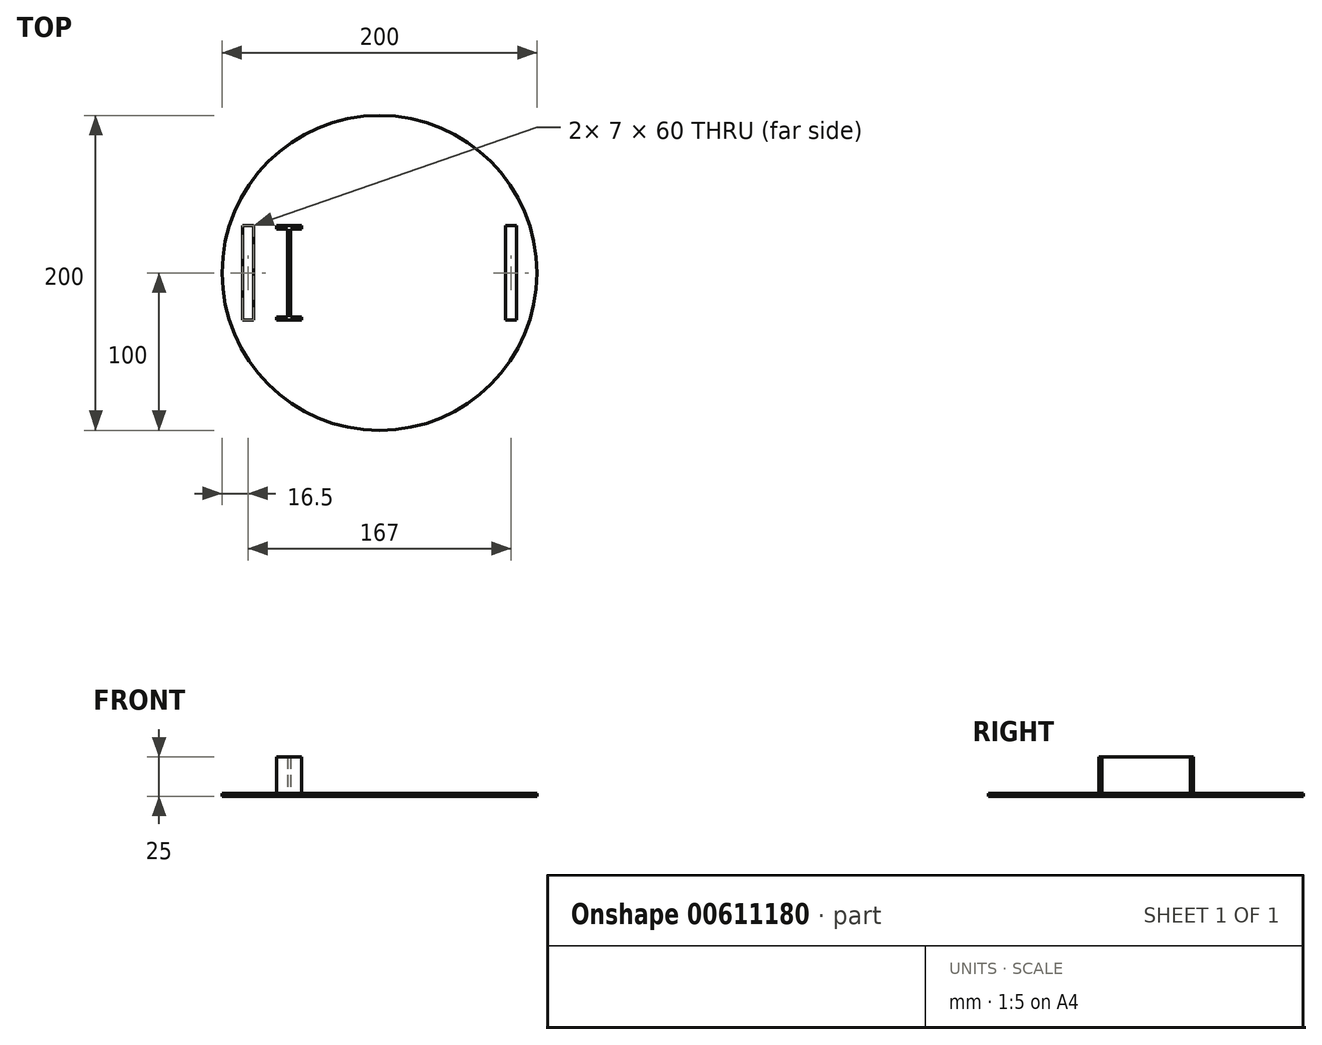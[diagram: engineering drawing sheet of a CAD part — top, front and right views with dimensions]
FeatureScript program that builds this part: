
annotation { "Feature Type Name" : "Feature", "Feature Type Description" : "" }
export const myFeature = defineFeature(function(context is Context, id is Id, definition is map)
    precondition{}
    {
        {
            var Q0;
            Q0=qCreatedBy(makeId("Top.planeOp"),FACE);
            var sketch = newSketch(context, id + "F0", { "sketchPlane" : qUnion([Q0])});
            skCircle(sketch, "E0", {"center": v(0, 0) * mm, "radius": 100 * mm});
            skLineSegment(sketch, "E1.bottom", {"start": v(-80, 30) * mm, "end": v(-87, 30) * mm});
            skLineSegment(sketch, "E1.top", {"start": v(-80, -30) * mm, "end": v(-87, -30) * mm});
            skLineSegment(sketch, "E1.left", {"start": v(-80, 30) * mm, "end": v(-80, -30) * mm});
            skLineSegment(sketch, "E1.right", {"start": v(-87, 30) * mm, "end": v(-87, -30) * mm});
            skPoint(sketch, "E1.middle", {"position": v(-83.5, 0) * mm});
            skLineSegment(sketch, "E2.MirrorCS", {"start": v(80, 30) * mm, "end": v(87, 30) * mm});
            skLineSegment(sketch, "E3.MirrorCS", {"start": v(80, 30) * mm, "end": v(80, -30) * mm});
            skLineSegment(sketch, "E4.MirrorCS", {"start": v(80, -30) * mm, "end": v(87, -30) * mm});
            skLineSegment(sketch, "E5.MirrorCS", {"start": v(87, 30) * mm, "end": v(87, -30) * mm});
            skPoint(sketch, "E6.MirrorP", {"position": v(83.5, 0) * mm});
            skLineSegment(sketch, "E7.bottom", {"start": v(-56.5, 30) * mm, "end": v(-58.5, 30) * mm});
            skLineSegment(sketch, "E7.left", {"start": v(-56.5, 30) * mm, "end": v(-56.5, -30) * mm});
            skLineSegment(sketch, "E7.right", {"start": v(-58.5, 30) * mm, "end": v(-58.5, -30) * mm});
            skPoint(sketch, "E7.middle", {"position": v(-57.5, 0) * mm});
            skLineSegment(sketch, "E8.bottom", {"start": v(-65.5, 28) * mm, "end": v(-49.5, 28) * mm});
            skLineSegment(sketch, "E8.top", {"start": v(-65.5, 30) * mm, "end": v(-49.5, 30) * mm});
            skLineSegment(sketch, "E8.left", {"start": v(-65.5, 28) * mm, "end": v(-65.5, 30) * mm});
            skLineSegment(sketch, "E8.right", {"start": v(-49.5, 28) * mm, "end": v(-49.5, 30) * mm});
            skLineSegment(sketch, "E9.MirrorCS", {"start": v(-56.5, -30) * mm, "end": v(-58.5, -30) * mm});
            skLineSegment(sketch, "E10.MirrorCS", {"start": v(-65.5, -30) * mm, "end": v(-49.5, -30) * mm});
            skLineSegment(sketch, "E11.MirrorCS", {"start": v(-65.5, -28) * mm, "end": v(-49.5, -28) * mm});
            skLineSegment(sketch, "E12.MirrorCS", {"start": v(-49.5, -28) * mm, "end": v(-49.5, -30) * mm});
            skLineSegment(sketch, "E13.MirrorCS", {"start": v(-65.5, -28) * mm, "end": v(-65.5, -30) * mm});
            skSolve(sketch);
        }
        {
            var Q0;
            {var subQ0=sQuery(id+"F0.wireOp",EDGE,"K0GAp1Y4-Ixp0-aC1l-omNU-r5FszGDL7PR0.top");var subQ1=sQuery(id+"F0.wireOp",EDGE,"HqlQ3rIF-Y2ew-o2BC-WH6p-pxuWtE5EoVCb.left");var subQ2=makeQuery(id+"F0.imprint","INTERSECT",VERTEX,{"derivedFrom":[subQ1,subQ0]});Q0=makeQuery(id+"F0.imprint","IMPRINT",FACE,{"disambiguationData":[TD([[makeQuery(id+"F0.imprint","IMPRINT",EDGE,{"disambiguationData":[TD([[subQ2,-1.0]])],"derivedFrom":subQ1}),-1.0]])]});}
            var Q1;
            {var subQ5=sQuery(id+"F0.wireOp",EDGE,"K0GAp1Y4-Ixp0-aC1l-omNU-r5FszGDL7PR0.right");Q1=makeQuery(id+"F0.imprint","IMPRINT",FACE,{"disambiguationData":[TD([[makeQuery(id+"F0.imprint","IMPRINT",EDGE,{"derivedFrom":subQ5}),1.0]])]});}
            var Q2;
            {var subQ5=sQuery(id+"F0.wireOp",EDGE,"K0GAp1Y4-Ixp0-aC1l-omNU-r5FszGDL7PR0.left");Q2=makeQuery(id+"F0.imprint","IMPRINT",FACE,{"disambiguationData":[TD([[makeQuery(id+"F0.imprint","IMPRINT",EDGE,{"derivedFrom":subQ5}),-1.0]])]});}
            var Q3;
            {var subQ0=sQuery(id+"F0.wireOp",EDGE,"K0GAp1Y4-Ixp0-aC1l-omNU-r5FszGDL7PR0.bottom");var subQ1=sQuery(id+"F0.wireOp",EDGE,"HqlQ3rIF-Y2ew-o2BC-WH6p-pxuWtE5EoVCb.left");var subQ2=makeQuery(id+"F0.imprint","INTERSECT",VERTEX,{"derivedFrom":[subQ1,subQ0]});Q3=makeQuery(id+"F0.imprint","IMPRINT",FACE,{"disambiguationData":[TD([[makeQuery(id+"F0.imprint","IMPRINT",EDGE,{"disambiguationData":[TD([[subQ2,-1.0]])],"derivedFrom":subQ1}),-1.0]])]});}
            var Q4;
            Q4=makeQuery(id+"F0.imprint","IMPRINT",FACE,{"disambiguationData":[TD([[makeQuery(id+"F0.imprint","IMPRINT",EDGE,{"derivedFrom":sQuery(id+"F0.wireOp",EDGE,"E0")}),1.0]])]});
            var Q5;
            {var subQ5=sQuery(id+"F0.wireOp",EDGE,"2bd450b3-5e51-421b-8461-b64049ee1ff72.MirrorCS");Q5=makeQuery(id+"F0.imprint","IMPRINT",FACE,{"disambiguationData":[TD([[makeQuery(id+"F0.imprint","IMPRINT",EDGE,{"derivedFrom":subQ5}),-1.0]])]});}
            var Q6;
            {var subQ0=sQuery(id+"F0.wireOp",EDGE,"2bd450b3-5e51-421b-8461-b64049ee1ff74.MirrorCS");var subQ1=sQuery(id+"F0.wireOp",EDGE,"HqlQ3rIF-Y2ew-o2BC-WH6p-pxuWtE5EoVCb.left");var subQ2=makeQuery(id+"F0.imprint","INTERSECT",VERTEX,{"derivedFrom":[subQ1,subQ0]});Q6=makeQuery(id+"F0.imprint","IMPRINT",FACE,{"disambiguationData":[TD([[makeQuery(id+"F0.imprint","IMPRINT",EDGE,{"disambiguationData":[TD([[subQ2,1.0]])],"derivedFrom":subQ1}),-1.0]])]});}
            var Q7;
            {var subQ5=sQuery(id+"F0.wireOp",EDGE,"2bd450b3-5e51-421b-8461-b64049ee1ff70.MirrorCS");Q7=makeQuery(id+"F0.imprint","IMPRINT",FACE,{"disambiguationData":[TD([[makeQuery(id+"F0.imprint","IMPRINT",EDGE,{"derivedFrom":subQ5}),1.0]])]});}
            var Q8;
            {var subQ5=sQuery(id+"F0.wireOp",EDGE,"E13.MirrorCS");Q8=makeQuery(id+"F0.imprint","IMPRINT",FACE,{"disambiguationData":[TD([[makeQuery(id+"F0.imprint","IMPRINT",EDGE,{"derivedFrom":subQ5}),1.0]])]});}
            var Q9;
            {var subQ0=sQuery(id+"F0.wireOp",EDGE,"E10.MirrorCS");var subQ1=sQuery(id+"F0.wireOp",EDGE,"E7.left");var subQ2=makeQuery(id+"F0.imprint","INTERSECT",VERTEX,{"derivedFrom":[subQ1,subQ0]});Q9=makeQuery(id+"F0.imprint","IMPRINT",FACE,{"disambiguationData":[TD([[makeQuery(id+"F0.imprint","IMPRINT",EDGE,{"disambiguationData":[TD([[subQ2,1.0]])],"derivedFrom":subQ1}),-1.0]])]});}
            var Q10;
            {var subQ5=sQuery(id+"F0.wireOp",EDGE,"E12.MirrorCS");Q10=makeQuery(id+"F0.imprint","IMPRINT",FACE,{"disambiguationData":[TD([[makeQuery(id+"F0.imprint","IMPRINT",EDGE,{"derivedFrom":subQ5}),-1.0]])]});}
            var Q11;
            {var subQ0=sQuery(id+"F0.wireOp",EDGE,"E8.bottom");var subQ1=sQuery(id+"F0.wireOp",EDGE,"E7.left");var subQ2=makeQuery(id+"F0.imprint","INTERSECT",VERTEX,{"derivedFrom":[subQ1,subQ0]});Q11=makeQuery(id+"F0.imprint","IMPRINT",FACE,{"disambiguationData":[TD([[makeQuery(id+"F0.imprint","IMPRINT",EDGE,{"disambiguationData":[TD([[subQ2,-1.0]])],"derivedFrom":subQ1}),-1.0]])]});}
            var Q12;
            {var subQ5=sQuery(id+"F0.wireOp",EDGE,"E8.left");Q12=makeQuery(id+"F0.imprint","IMPRINT",FACE,{"disambiguationData":[TD([[makeQuery(id+"F0.imprint","IMPRINT",EDGE,{"derivedFrom":subQ5}),-1.0]])]});}
            var Q13;
            {var subQ0=sQuery(id+"F0.wireOp",EDGE,"E8.top");var subQ1=sQuery(id+"F0.wireOp",EDGE,"E7.left");var subQ2=makeQuery(id+"F0.imprint","INTERSECT",VERTEX,{"derivedFrom":[subQ1,subQ0]});Q13=makeQuery(id+"F0.imprint","IMPRINT",FACE,{"disambiguationData":[TD([[makeQuery(id+"F0.imprint","IMPRINT",EDGE,{"disambiguationData":[TD([[subQ2,-1.0]])],"derivedFrom":subQ1}),-1.0]])]});}
            var Q14;
            {var subQ5=sQuery(id+"F0.wireOp",EDGE,"E8.right");Q14=makeQuery(id+"F0.imprint","IMPRINT",FACE,{"disambiguationData":[TD([[makeQuery(id+"F0.imprint","IMPRINT",EDGE,{"derivedFrom":subQ5}),1.0]])]});}
            extrude(context, id + "F1", {"entities" : qUnion([Q0, Q1, Q2, Q3, Q4, Q5, Q6, Q7, Q8, Q9, Q10, Q11, Q12, Q13, Q14]), "depth" : 2 * mm, "offsetDistance" : 25.4 * mm});
        }
        {
            var Q0;
            {var subQ5=sQuery(id+"F0.wireOp",EDGE,"E8.left");Q0=makeQuery(id+"F0.imprint","IMPRINT",FACE,{"disambiguationData":[TD([[makeQuery(id+"F0.imprint","IMPRINT",EDGE,{"derivedFrom":subQ5}),-1.0]])]});}
            var Q1;
            {var subQ0=sQuery(id+"F0.wireOp",EDGE,"E8.top");var subQ1=sQuery(id+"F0.wireOp",EDGE,"E7.left");var subQ2=makeQuery(id+"F0.imprint","INTERSECT",VERTEX,{"derivedFrom":[subQ1,subQ0]});Q1=makeQuery(id+"F0.imprint","IMPRINT",FACE,{"disambiguationData":[TD([[makeQuery(id+"F0.imprint","IMPRINT",EDGE,{"disambiguationData":[TD([[subQ2,-1.0]])],"derivedFrom":subQ1}),-1.0]])]});}
            var Q2;
            {var subQ5=sQuery(id+"F0.wireOp",EDGE,"E8.right");Q2=makeQuery(id+"F0.imprint","IMPRINT",FACE,{"disambiguationData":[TD([[makeQuery(id+"F0.imprint","IMPRINT",EDGE,{"derivedFrom":subQ5}),1.0]])]});}
            var Q3;
            {var subQ0=sQuery(id+"F0.wireOp",EDGE,"E8.bottom");var subQ1=sQuery(id+"F0.wireOp",EDGE,"E7.left");var subQ2=makeQuery(id+"F0.imprint","INTERSECT",VERTEX,{"derivedFrom":[subQ1,subQ0]});Q3=makeQuery(id+"F0.imprint","IMPRINT",FACE,{"disambiguationData":[TD([[makeQuery(id+"F0.imprint","IMPRINT",EDGE,{"disambiguationData":[TD([[subQ2,-1.0]])],"derivedFrom":subQ1}),-1.0]])]});}
            var Q4;
            {var subQ5=sQuery(id+"F0.wireOp",EDGE,"E13.MirrorCS");Q4=makeQuery(id+"F0.imprint","IMPRINT",FACE,{"disambiguationData":[TD([[makeQuery(id+"F0.imprint","IMPRINT",EDGE,{"derivedFrom":subQ5}),1.0]])]});}
            var Q5;
            {var subQ0=sQuery(id+"F0.wireOp",EDGE,"E10.MirrorCS");var subQ1=sQuery(id+"F0.wireOp",EDGE,"E7.left");var subQ2=makeQuery(id+"F0.imprint","INTERSECT",VERTEX,{"derivedFrom":[subQ1,subQ0]});Q5=makeQuery(id+"F0.imprint","IMPRINT",FACE,{"disambiguationData":[TD([[makeQuery(id+"F0.imprint","IMPRINT",EDGE,{"disambiguationData":[TD([[subQ2,1.0]])],"derivedFrom":subQ1}),-1.0]])]});}
            var Q6;
            {var subQ5=sQuery(id+"F0.wireOp",EDGE,"E12.MirrorCS");Q6=makeQuery(id+"F0.imprint","IMPRINT",FACE,{"disambiguationData":[TD([[makeQuery(id+"F0.imprint","IMPRINT",EDGE,{"derivedFrom":subQ5}),-1.0]])]});}
            extrude(context, id + "F2", {"entities" : qUnion([Q0, Q1, Q2, Q3, Q4, Q5, Q6]), "operationType" : NewBodyOperationType.ADD, "depth" : 25 * mm, "offsetDistance" : 25 * mm});
        }
    });
